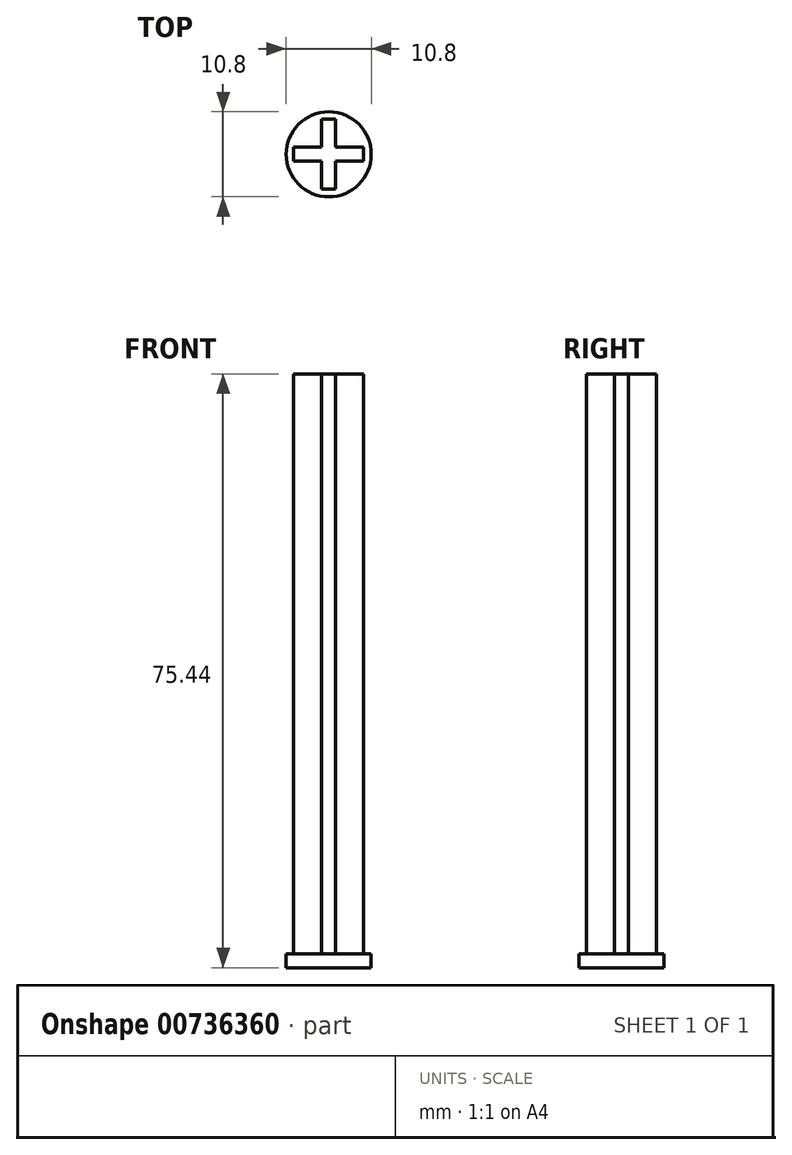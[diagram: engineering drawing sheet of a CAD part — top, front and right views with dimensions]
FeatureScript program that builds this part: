
annotation { "Feature Type Name" : "Feature", "Feature Type Description" : "" }
export const myFeature = defineFeature(function(context is Context, id is Id, definition is map)
    precondition{}
    {
        {
            var Q0;
            Q0=qCreatedBy(makeId("Top.planeOp"),FACE);
            var sketch = newSketch(context, id + "F0", { "sketchPlane" : qUnion([Q0])});
            skLineSegment(sketch, "E0", {"start": v(-0.89, 4.45) * mm, "end": v(-0.89, 0.89) * mm});
            skLineSegment(sketch, "E1", {"start": v(-0.89, 0.89) * mm, "end": v(-4.45, 0.89) * mm});
            skLineSegment(sketch, "E2", {"start": v(-4.45, 0.89) * mm, "end": v(-4.45, -0.89) * mm});
            skLineSegment(sketch, "E3", {"start": v(-4.45, -0.89) * mm, "end": v(-0.89, -0.89) * mm});
            skLineSegment(sketch, "E4", {"start": v(-0.89, -0.89) * mm, "end": v(-0.89, -4.45) * mm});
            skLineSegment(sketch, "E5", {"start": v(-0.89, -4.45) * mm, "end": v(0.89, -4.45) * mm});
            skLineSegment(sketch, "E6", {"start": v(0.89, -4.45) * mm, "end": v(0.89, -0.89) * mm});
            skLineSegment(sketch, "E7", {"start": v(0.89, -0.89) * mm, "end": v(4.45, -0.89) * mm});
            skLineSegment(sketch, "E8", {"start": v(4.45, -0.89) * mm, "end": v(4.45, 0.89) * mm});
            skLineSegment(sketch, "E9", {"start": v(4.45, 0.89) * mm, "end": v(0.89, 0.89) * mm});
            skLineSegment(sketch, "E10", {"start": v(0.89, 0.89) * mm, "end": v(0.89, 4.45) * mm});
            skLineSegment(sketch, "E11", {"start": v(0.89, 4.45) * mm, "end": v(-0.89, 4.45) * mm});
            skLineSegment(sketch, "E12", {"start": v(0, 4.45) * mm, "end": v(0, -4.45) * mm, "construction": true});
            skLineSegment(sketch, "E13", {"start": v(-4.45, 0) * mm, "end": v(4.45, 0) * mm, "construction": true});
            skSolve(sketch);
        }
        {
            var Q0;
            Q0 = qSketchRegion(id + "F0", true);
            extrude(context, id + "F1", {"entities" : qUnion([Q0]), "depth" : 73.66 * mm, "offsetDistance" : 25.4 * mm});
        }
        {
            var Q0;
            Q0=qCreatedBy(makeId("Top.planeOp"),FACE);
            var sketch = newSketch(context, id + "F2", { "sketchPlane" : qUnion([Q0])});
            skCircle(sketch, "E14", {"center": v(0, 0) * mm, "radius": 5.4 * mm});
            skSolve(sketch);
        }
        {
            var Q0;
            Q0 = qSketchRegion(id + "F2", true);
            extrude(context, id + "F3", {"entities" : qUnion([Q0]), "operationType" : NewBodyOperationType.ADD, "oppositeDirection" : true, "depth" : 1.78 * mm, "offsetDistance" : 25.4 * mm});
        }
    });
